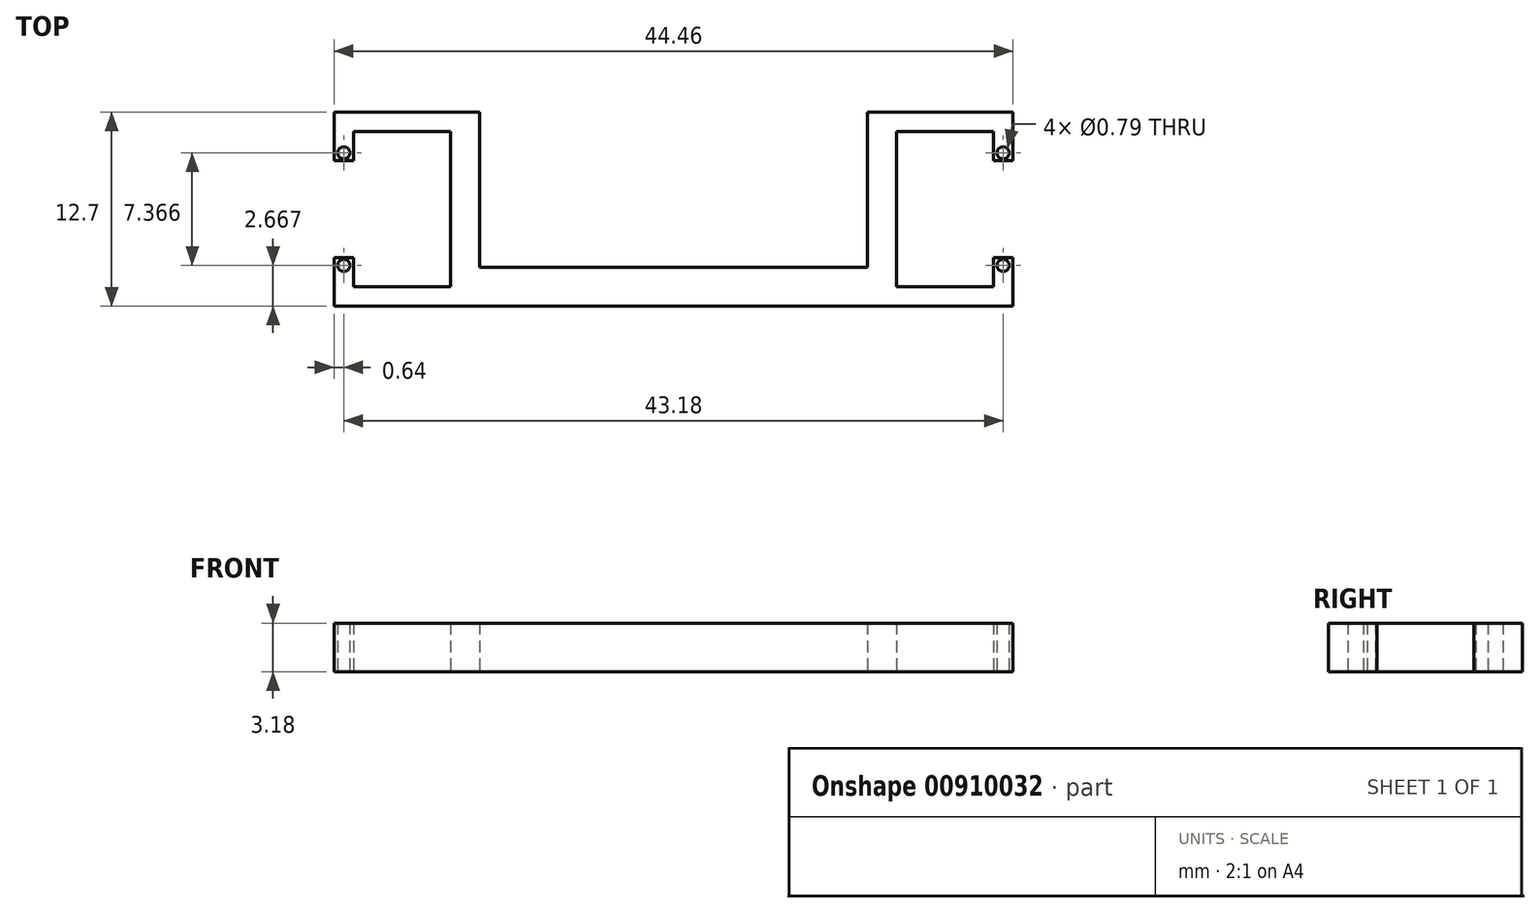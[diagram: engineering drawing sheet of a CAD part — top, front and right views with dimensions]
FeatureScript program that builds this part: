
annotation { "Feature Type Name" : "Feature", "Feature Type Description" : "" }
export const myFeature = defineFeature(function(context is Context, id is Id, definition is map)
    precondition{}
    {
        {
            var Q0;
            Q0=qCreatedBy(makeId("Top.planeOp"),FACE);
            var sketch = newSketch(context, id + "F0", { "sketchPlane" : qUnion([Q0])});
            skLineSegment(sketch, "E0", {"start": v(-22.23, 11.43) * mm, "end": v(-12.7, 11.43) * mm});
            skLineSegment(sketch, "E1", {"start": v(-12.7, 11.43) * mm, "end": v(-12.7, -1.27) * mm});
            skLineSegment(sketch, "E2", {"start": v(-12.7, -1.27) * mm, "end": v(-22.23, -1.27) * mm});
            skLineSegment(sketch, "E3", {"start": v(-22.23, -1.27) * mm, "end": v(-22.23, 1.9) * mm});
            skLineSegment(sketch, "E4", {"start": v(-22.23, 1.9) * mm, "end": v(-20.96, 1.9) * mm});
            skLineSegment(sketch, "E5", {"start": v(-20.96, 1.9) * mm, "end": v(-20.96, 0) * mm});
            skLineSegment(sketch, "E6", {"start": v(-20.96, 0) * mm, "end": v(-14.6, 0) * mm});
            skLineSegment(sketch, "E7", {"start": v(-14.6, 0) * mm, "end": v(-14.6, 10.16) * mm});
            skLineSegment(sketch, "E8", {"start": v(-14.6, 10.16) * mm, "end": v(-20.96, 10.16) * mm});
            skLineSegment(sketch, "E9", {"start": v(-20.96, 10.16) * mm, "end": v(-20.96, 8.26) * mm});
            skLineSegment(sketch, "E10", {"start": v(-20.96, 8.25) * mm, "end": v(-22.23, 8.25) * mm});
            skLineSegment(sketch, "E11", {"start": v(-22.23, 8.26) * mm, "end": v(-22.23, 11.43) * mm});
            skLineSegment(sketch, "E12.MirrorCS", {"start": v(14.6, 0) * mm, "end": v(14.6, 10.16) * mm});
            skLineSegment(sketch, "E13.MirrorCS", {"start": v(12.7, 11.43) * mm, "end": v(12.7, -1.27) * mm});
            skLineSegment(sketch, "E14.MirrorCS", {"start": v(20.96, 0) * mm, "end": v(14.6, 0) * mm});
            skLineSegment(sketch, "E15.MirrorCS", {"start": v(12.7, -1.27) * mm, "end": v(22.23, -1.27) * mm});
            skLineSegment(sketch, "E16.MirrorCS", {"start": v(22.23, -1.27) * mm, "end": v(22.23, 1.9) * mm});
            skLineSegment(sketch, "E17.MirrorCS", {"start": v(20.96, 1.9) * mm, "end": v(20.96, 0) * mm});
            skLineSegment(sketch, "E18.MirrorCS", {"start": v(22.23, 1.9) * mm, "end": v(20.96, 1.9) * mm});
            skLineSegment(sketch, "E19.MirrorCS", {"start": v(20.96, 8.25) * mm, "end": v(22.23, 8.25) * mm});
            skLineSegment(sketch, "E20.MirrorCS", {"start": v(22.23, 8.26) * mm, "end": v(22.23, 11.43) * mm});
            skLineSegment(sketch, "E21.MirrorCS", {"start": v(20.96, 10.16) * mm, "end": v(20.96, 8.26) * mm});
            skLineSegment(sketch, "E22.MirrorCS", {"start": v(14.6, 10.16) * mm, "end": v(20.96, 10.16) * mm});
            skLineSegment(sketch, "E23.MirrorCS", {"start": v(22.23, 11.43) * mm, "end": v(12.7, 11.43) * mm});
            skCircle(sketch, "E24", {"center": v(-21.6, 8.76) * mm, "radius": 0.4 * mm});
            skCircle(sketch, "E25", {"center": v(-21.6, 1.4) * mm, "radius": 0.4 * mm});
            skCircle(sketch, "E26.MirrorC", {"center": v(21.6, 8.76) * mm, "radius": 0.4 * mm});
            skCircle(sketch, "E27.MirrorC", {"center": v(21.6, 1.4) * mm, "radius": 0.4 * mm});
            skLineSegment(sketch, "E28", {"start": v(-12.7, 1.27) * mm, "end": v(12.7, 1.27) * mm});
            skLineSegment(sketch, "E29", {"start": v(-12.7, -1.27) * mm, "end": v(12.7, -1.27) * mm});
            skCircle(sketch, "E30", {"center": v(0, -64.77) * mm, "radius": 0.8 * mm});
            skPoint(sketch, "E31.visualSharp", {"position": v(0, -71.12) * mm});
            skArc(sketch, "E32.filletArc", {"start": v(-0.62, -67.68) * mm, "mid": v(0, -68.2) * mm, "end": v(0.62, -67.68) * mm});
            skSolve(sketch);
        }
        {
            var Q0;
            {var subQ0=sQuery(id+"F0.wireOp",EDGE,"E0");Q0=makeQuery(id+"F0.imprint","IMPRINT",FACE,{"disambiguationData":[TD([[makeQuery(id+"F0.imprint","IMPRINT",EDGE,{"derivedFrom":subQ0}),-1.0]])]});}
            var Q1;
            {var subQ4=sQuery(id+"F0.wireOp",EDGE,"E28");Q1=makeQuery(id+"F0.imprint","IMPRINT",FACE,{"disambiguationData":[TD([[makeQuery(id+"F0.imprint","IMPRINT",EDGE,{"derivedFrom":subQ4}),-1.0]])]});}
            var Q2;
            Q2=makeQuery(id+"F0.imprint","IMPRINT",FACE,{"disambiguationData":[TD([[makeQuery(id+"F0.imprint","IMPRINT",EDGE,{"derivedFrom":sQuery(id+"F0.wireOp",EDGE,"E12.MirrorCS")}),1.0]])]});
            var Q3;
            {var subQ8=sQuery(id+"F0.wireOp",EDGE,"1PjGuBIR-9Pv4-rMLk-RCzl-I51GPpE8k7TI");Q3=makeQuery(id+"F0.imprint","IMPRINT",FACE,{"disambiguationData":[TD([[makeQuery(id+"F0.imprint","IMPRINT",EDGE,{"derivedFrom":subQ8}),1.0]])]});}
            var Q4;
            {var subQ0=sQuery(id+"F0.wireOp",EDGE,"OXakiHan-UgVx-rdoX-cPiA-IruJlf0qgsDQ");Q4=makeQuery(id+"F0.imprint","IMPRINT",FACE,{"disambiguationData":[TD([[makeQuery(id+"F0.imprint","IMPRINT",EDGE,{"derivedFrom":subQ0}),1.0]])]});}
            var Q5;
            {var subQ0=sQuery(id+"F0.wireOp",EDGE,"OmNe6PKq-3gdd-MlfY-zTIg-1ZM3LVirDwKM");Q5=makeQuery(id+"F0.imprint","IMPRINT",FACE,{"disambiguationData":[TD([[makeQuery(id+"F0.imprint","IMPRINT",EDGE,{"derivedFrom":subQ0}),1.0]])]});}
            extrude(context, id + "F1", {"entities" : qUnion([Q0, Q1, Q2, Q3, Q4, Q5]), "depth" : 3.17 * mm, "offsetDistance" : 25.4 * mm});
        }
    });
